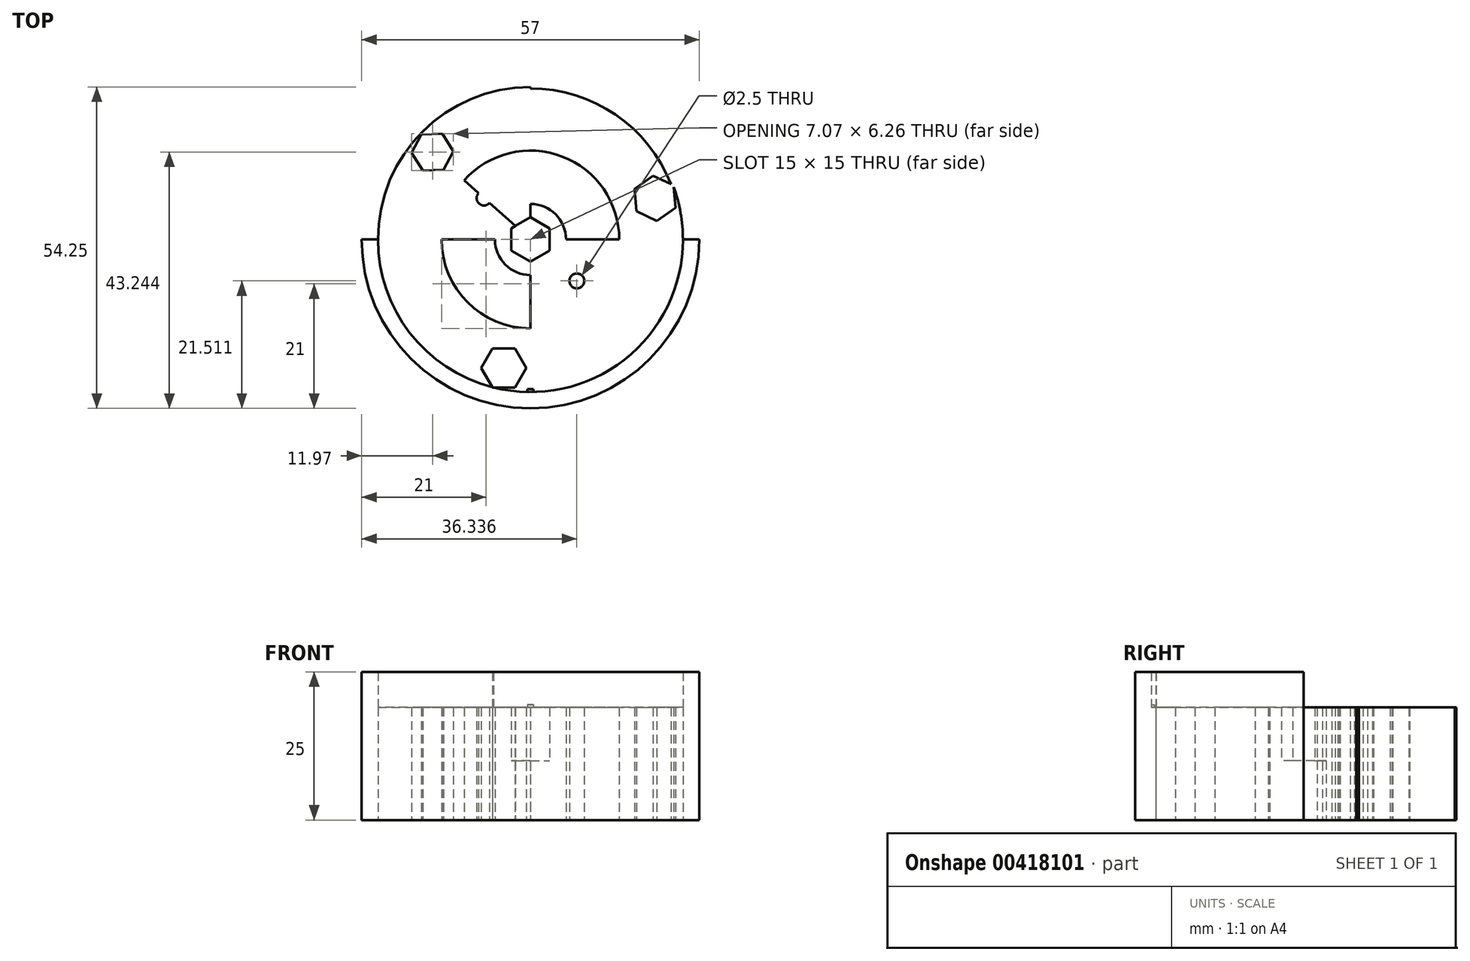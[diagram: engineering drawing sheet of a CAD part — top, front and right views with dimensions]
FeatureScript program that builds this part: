
annotation { "Feature Type Name" : "Feature", "Feature Type Description" : "" }
export const myFeature = defineFeature(function(context is Context, id is Id, definition is map)
    precondition{}
    {
        {
            var Q0;
            Q0=qCreatedBy(makeId("Top.planeOp"),FACE);
            var sketch = newSketch(context, id + "F0", { "sketchPlane" : qUnion([Q0])});
            skCircle(sketch, "E0", {"center": v(0, 0) * mm, "radius": 25.5 * mm});
            skCircle(sketch, "E1", {"center": v(0, 0) * mm, "radius": 25.75 * mm});
            skCircle(sketch, "E2", {"center": v(0, 0) * mm, "radius": 28.5 * mm});
            skLineSegment(sketch, "E3", {"start": v(0, 0) * mm, "end": v(0, 28.5) * mm});
            skLineSegment(sketch, "E4", {"start": v(0, 28.5) * mm, "end": v(0, -28.5) * mm});
            skLineSegment(sketch, "E5", {"start": v(-28.5, 0) * mm, "end": v(28.5, 0) * mm});
            skLineSegment(sketch, "E6", {"start": v(0, 0) * mm, "end": v(-4.5, -21.69) * mm});
            skLineSegment(sketch, "E7", {"start": v(-4.5, -21.69) * mm, "end": v(0, -22.62) * mm});
            skLineSegment(sketch, "E8", {"start": v(0, 0) * mm, "end": v(-16.53, 14.74) * mm});
            skLineSegment(sketch, "E9", {"start": v(-16.53, 14.74) * mm, "end": v(0, 0) * mm});
            skLineSegment(sketch, "E10", {"start": v(0, 0) * mm, "end": v(21.03, 6.94) * mm});
            skCircle(sketch, "E11", {"center": v(-4.5, -21.69) * mm, "radius": 0.75 * mm});
            skCircle(sketch, "E12", {"center": v(21.03, 6.94) * mm, "radius": 0.75 * mm});
            skCircle(sketch, "E13", {"center": v(-16.53, 14.74) * mm, "radius": 0.75 * mm});
            skCircle(sketch, "E14.cCircle", {"center": v(0, 0) * mm, "radius": 3.25 * mm, "construction": true});
            skLineSegment(sketch, "E14.0", {"start": v(3.25, 1.88) * mm, "end": v(3.25, -1.88) * mm});
            skLineSegment(sketch, "E14.1", {"start": v(3.25, -1.88) * mm, "end": v(0, -3.75) * mm});
            skLineSegment(sketch, "E14.2", {"start": v(0, -3.75) * mm, "end": v(-3.25, -1.88) * mm});
            skLineSegment(sketch, "E14.3", {"start": v(-3.25, -1.88) * mm, "end": v(-3.25, 1.88) * mm});
            skLineSegment(sketch, "E14.4", {"start": v(-3.25, 1.88) * mm, "end": v(0, 3.75) * mm});
            skLineSegment(sketch, "E14.5", {"start": v(0, 3.75) * mm, "end": v(3.25, 1.88) * mm});
            skPoint(sketch, "E14.0.midPoint", {"position": v(3.25, 0) * mm});
            skCircle(sketch, "E15", {"center": v(0, 0) * mm, "radius": 6 * mm});
            skCircle(sketch, "E16", {"center": v(0, 0) * mm, "radius": 15 * mm});
            skLineSegment(sketch, "E17", {"start": v(-9.73, -23.84) * mm, "end": v(-9.73, -26.79) * mm});
            skLineSegment(sketch, "E18", {"start": v(8.49, -27.2) * mm, "end": v(8.49, -24.31) * mm});
            skCircle(sketch, "E19.cCircle", {"center": v(-16.53, 14.74) * mm, "radius": 3.06 * mm, "construction": true});
            skLineSegment(sketch, "E19.0", {"start": v(-14.88, 17.87) * mm, "end": v(-13, 14.88) * mm});
            skLineSegment(sketch, "E19.1", {"start": v(-13, 14.88) * mm, "end": v(-14.65, 11.75) * mm});
            skLineSegment(sketch, "E19.2", {"start": v(-14.65, 11.75) * mm, "end": v(-18.18, 11.62) * mm});
            skLineSegment(sketch, "E19.3", {"start": v(-18.18, 11.62) * mm, "end": v(-20.06, 14.6) * mm});
            skLineSegment(sketch, "E19.4", {"start": v(-20.06, 14.6) * mm, "end": v(-18.41, 17.74) * mm});
            skLineSegment(sketch, "E19.5", {"start": v(-18.41, 17.74) * mm, "end": v(-14.88, 17.87) * mm});
            skPoint(sketch, "E19.0.midPoint", {"position": v(-13.94, 16.38) * mm});
            skCircle(sketch, "E20.cCircle", {"center": v(-4.5, -21.69) * mm, "radius": 3.3 * mm, "construction": true});
            skLineSegment(sketch, "E20.0", {"start": v(-6.4, -18.39) * mm, "end": v(-2.6, -18.39) * mm});
            skLineSegment(sketch, "E20.1", {"start": v(-2.6, -18.39) * mm, "end": v(-0.7, -21.69) * mm});
            skLineSegment(sketch, "E20.2", {"start": v(-0.7, -21.69) * mm, "end": v(-2.6, -24.99) * mm});
            skLineSegment(sketch, "E20.3", {"start": v(-2.6, -24.99) * mm, "end": v(-6.4, -24.99) * mm});
            skLineSegment(sketch, "E20.4", {"start": v(-6.4, -24.99) * mm, "end": v(-8.31, -21.69) * mm});
            skLineSegment(sketch, "E20.5", {"start": v(-8.31, -21.69) * mm, "end": v(-6.4, -18.39) * mm});
            skPoint(sketch, "E20.0.midPoint", {"position": v(-4.5, -18.39) * mm});
            skCircle(sketch, "E21.cCircle", {"center": v(21.03, 6.94) * mm, "radius": 3.3 * mm, "construction": true});
            skLineSegment(sketch, "E21.0", {"start": v(20.7, 10.74) * mm, "end": v(24.16, 9.12) * mm});
            skLineSegment(sketch, "E21.1", {"start": v(24.16, 9.12) * mm, "end": v(24.49, 5.33) * mm});
            skLineSegment(sketch, "E21.2", {"start": v(24.49, 5.33) * mm, "end": v(21.36, 3.15) * mm});
            skLineSegment(sketch, "E21.3", {"start": v(21.36, 3.15) * mm, "end": v(17.9, 4.76) * mm});
            skLineSegment(sketch, "E21.4", {"start": v(17.9, 4.76) * mm, "end": v(17.58, 8.56) * mm});
            skLineSegment(sketch, "E21.5", {"start": v(17.58, 8.56) * mm, "end": v(20.7, 10.74) * mm});
            skPoint(sketch, "E21.0.midPoint", {"position": v(22.43, 9.93) * mm});
            skLineSegment(sketch, "E22", {"start": v(-4.48, 4) * mm, "end": v(-11.2, 9.98) * mm});
            skLineSegment(sketch, "E23", {"start": v(-11.2, 9.98) * mm, "end": v(11.2, -9.98) * mm});
            skLineSegment(sketch, "E24", {"start": v(11.2, -9.98) * mm, "end": v(0, 0) * mm});
            skCircle(sketch, "E25", {"center": v(-7.84, 6.99) * mm, "radius": 1.25 * mm});
            skLineSegment(sketch, "E26", {"start": v(11.2, -9.98) * mm, "end": v(4.48, -4) * mm});
            skCircle(sketch, "E27", {"center": v(7.84, -6.99) * mm, "radius": 1.25 * mm});
            skLineSegment(sketch, "E28", {"start": v(-0.5, -25.74) * mm, "end": v(-0.5, -25.24) * mm});
            skLineSegment(sketch, "E29", {"start": v(-0.5, -25.24) * mm, "end": v(0, -25.24) * mm});
            skLineSegment(sketch, "E30.MirrorCS", {"start": v(0.5, -25.24) * mm, "end": v(0, -25.24) * mm});
            skLineSegment(sketch, "E31.MirrorCS", {"start": v(0.5, -25.74) * mm, "end": v(0.5, -25.24) * mm});
            skSolve(sketch);
        }
        {
            var Q0;
            {var subQ0=sQuery(id+"F0.wireOp",EDGE,"E16");var subQ1=sQuery(id+"F0.wireOp",EDGE,"E5");var subQ2=makeQuery(id+"F0.imprint","INTERSECT",VERTEX,{"disambiguationData":[OD(0.0)],"derivedFrom":[subQ1,subQ0]});Q0=makeQuery(id+"F0.imprint","IMPRINT",FACE,{"disambiguationData":[TD([[makeQuery(id+"F0.imprint","IMPRINT",EDGE,{"disambiguationData":[TD([[subQ2,-1.0]])],"derivedFrom":subQ1}),1.0]])]});}
            var Q1;
            {var subQ0=sQuery(id+"F0.wireOp",EDGE,"E4");var subQ1=sQuery(id+"F0.wireOp",EDGE,"E1");var subQ2=makeQuery(id+"F0.imprint","INTERSECT",VERTEX,{"disambiguationData":[OD(0.0)],"derivedFrom":[subQ1,subQ0]});Q1=makeQuery(id+"F0.imprint","IMPRINT",FACE,{"disambiguationData":[TD([[makeQuery(id+"F0.imprint","IMPRINT",EDGE,{"disambiguationData":[TD([[subQ2,1.0]])],"derivedFrom":subQ1}),-1.0]])]});}
            var Q2;
            {var subQ0=sQuery(id+"F0.wireOp",EDGE,"E4");var subQ1=sQuery(id+"F0.wireOp",EDGE,"E1");var subQ2=makeQuery(id+"F0.imprint","INTERSECT",VERTEX,{"disambiguationData":[OD(0.0)],"derivedFrom":[subQ1,subQ0]});Q2=makeQuery(id+"F0.imprint","IMPRINT",FACE,{"disambiguationData":[TD([[makeQuery(id+"F0.imprint","IMPRINT",EDGE,{"disambiguationData":[TD([[subQ2,-1.0]])],"derivedFrom":subQ1}),-1.0]])]});}
            var Q3;
            {var subQ0=sQuery(id+"F0.wireOp",EDGE,"E17");Q3=makeQuery(id+"F0.imprint","IMPRINT",FACE,{"disambiguationData":[TD([[makeQuery(id+"F0.imprint","IMPRINT",EDGE,{"derivedFrom":subQ0}),-1.0]])]});}
            var Q4;
            {var subQ0=sQuery(id+"F0.wireOp",EDGE,"E17");Q4=makeQuery(id+"F0.imprint","IMPRINT",FACE,{"disambiguationData":[TD([[makeQuery(id+"F0.imprint","IMPRINT",EDGE,{"derivedFrom":subQ0}),1.0]])]});}
            var Q5;
            {var subQ0=sQuery(id+"F0.wireOp",EDGE,"E18");Q5=makeQuery(id+"F0.imprint","IMPRINT",FACE,{"disambiguationData":[TD([[makeQuery(id+"F0.imprint","IMPRINT",EDGE,{"derivedFrom":subQ0}),1.0]])]});}
            var Q6;
            {var subQ0=sQuery(id+"F0.wireOp",EDGE,"E18");Q6=makeQuery(id+"F0.imprint","IMPRINT",FACE,{"disambiguationData":[TD([[makeQuery(id+"F0.imprint","IMPRINT",EDGE,{"derivedFrom":subQ0}),-1.0]])]});}
            var Q7;
            {var subQ5=sQuery(id+"F0.wireOp",EDGE,"E5");var subQ6=sQuery(id+"F0.wireOp",EDGE,"E0");var subQ7=makeQuery(id+"F0.imprint","INTERSECT",VERTEX,{"disambiguationData":[OD(1.0)],"derivedFrom":[subQ6,subQ5]});Q7=makeQuery(id+"F0.imprint","IMPRINT",FACE,{"disambiguationData":[TD([[makeQuery(id+"F0.imprint","IMPRINT",EDGE,{"disambiguationData":[TD([[subQ7,-1.0]])],"derivedFrom":subQ6}),1.0]])]});}
            var Q8;
            {var subQ2=sQuery(id+"F0.wireOp",EDGE,"E0");var subQ6=sQuery(id+"F0.wireOp",EDGE,"E5");var subQ7=makeQuery(id+"F0.imprint","INTERSECT",VERTEX,{"disambiguationData":[OD(0.0)],"derivedFrom":[subQ2,subQ6]});Q8=makeQuery(id+"F0.imprint","IMPRINT",FACE,{"disambiguationData":[TD([[makeQuery(id+"F0.imprint","IMPRINT",EDGE,{"disambiguationData":[TD([[subQ7,1.0]])],"derivedFrom":subQ2}),1.0]])]});}
            var Q9;
            {var subQ0=sQuery(id+"F0.wireOp",EDGE,"E7");var subQ1=sQuery(id+"F0.wireOp",EDGE,"E4");var subQ2=makeQuery(id+"F0.imprint","INTERSECT",VERTEX,{"derivedFrom":[subQ1,subQ0]});Q9=makeQuery(id+"F0.imprint","IMPRINT",FACE,{"disambiguationData":[TD([[makeQuery(id+"F0.imprint","IMPRINT",EDGE,{"disambiguationData":[TD([[subQ2,1.0]])],"derivedFrom":subQ1}),-1.0]])]});}
            var Q10;
            {var subQ0=sQuery(id+"F0.wireOp",EDGE,"E15");var subQ1=sQuery(id+"F0.wireOp",EDGE,"E4");var subQ2=makeQuery(id+"F0.imprint","INTERSECT",VERTEX,{"disambiguationData":[OD(1.0)],"derivedFrom":[subQ1,subQ0]});Q10=makeQuery(id+"F0.imprint","IMPRINT",FACE,{"disambiguationData":[TD([[makeQuery(id+"F0.imprint","IMPRINT",EDGE,{"disambiguationData":[TD([[subQ2,-1.0]])],"derivedFrom":subQ1}),1.0]])]});}
            var Q11;
            {var subQ0=sQuery(id+"F0.wireOp",EDGE,"E16");var subQ1=sQuery(id+"F0.wireOp",EDGE,"E4");var subQ2=makeQuery(id+"F0.imprint","INTERSECT",VERTEX,{"disambiguationData":[OD(0.0)],"derivedFrom":[subQ1,subQ0]});Q11=makeQuery(id+"F0.imprint","IMPRINT",FACE,{"disambiguationData":[TD([[makeQuery(id+"F0.imprint","IMPRINT",EDGE,{"disambiguationData":[TD([[subQ2,-1.0]])],"derivedFrom":subQ1}),-1.0]])]});}
            var Q12;
            {var subQ0=sQuery(id+"F0.wireOp",EDGE,"E14.5");Q12=makeQuery(id+"F0.imprint","IMPRINT",FACE,{"disambiguationData":[TD([[makeQuery(id+"F0.imprint","IMPRINT",EDGE,{"derivedFrom":subQ0}),1.0]])]});}
            var Q13;
            {var subQ0=sQuery(id+"F0.wireOp",EDGE,"E14.5");Q13=makeQuery(id+"F0.imprint","IMPRINT",FACE,{"disambiguationData":[TD([[makeQuery(id+"F0.imprint","IMPRINT",EDGE,{"derivedFrom":subQ0}),1.0]])]});}
            var Q14;
            {var subQ0=sQuery(id+"F0.wireOp",EDGE,"E14.1");Q14=makeQuery(id+"F0.imprint","IMPRINT",FACE,{"disambiguationData":[TD([[makeQuery(id+"F0.imprint","IMPRINT",EDGE,{"derivedFrom":subQ0}),1.0]])]});}
            var Q15;
            {var subQ0=sQuery(id+"F0.wireOp",EDGE,"E14.1");Q15=makeQuery(id+"F0.imprint","IMPRINT",FACE,{"disambiguationData":[TD([[makeQuery(id+"F0.imprint","IMPRINT",EDGE,{"derivedFrom":subQ0}),1.0]])]});}
            var Q16;
            {var subQ3=sQuery(id+"F0.wireOp",EDGE,"E5");var subQ7=sQuery(id+"F0.wireOp",EDGE,"E15");var subQ9=makeQuery(id+"F0.imprint","INTERSECT",VERTEX,{"disambiguationData":[OD(0.0)],"derivedFrom":[subQ3,subQ7]});Q16=makeQuery(id+"F0.imprint","IMPRINT",FACE,{"disambiguationData":[TD([[makeQuery(id+"F0.imprint","IMPRINT",EDGE,{"disambiguationData":[TD([[subQ9,-1.0]])],"derivedFrom":subQ3}),-1.0]])]});}
            var Q17;
            {var subQ0=sQuery(id+"F0.wireOp",EDGE,"E14.2");var subQ5=sQuery(id+"F0.wireOp",EDGE,"E6");var subQ6=makeQuery(id+"F0.imprint","INTERSECT",VERTEX,{"derivedFrom":[subQ5,subQ0]});Q17=makeQuery(id+"F0.imprint","IMPRINT",FACE,{"disambiguationData":[TD([[makeQuery(id+"F0.imprint","IMPRINT",EDGE,{"disambiguationData":[TD([[subQ6,-1.0]])],"derivedFrom":subQ5}),1.0]])]});}
            var Q18;
            {var subQ3=sQuery(id+"F0.wireOp",EDGE,"E5");var subQ7=sQuery(id+"F0.wireOp",EDGE,"E15");var subQ9=makeQuery(id+"F0.imprint","INTERSECT",VERTEX,{"disambiguationData":[OD(0.0)],"derivedFrom":[subQ3,subQ7]});Q18=makeQuery(id+"F0.imprint","IMPRINT",FACE,{"disambiguationData":[TD([[makeQuery(id+"F0.imprint","IMPRINT",EDGE,{"disambiguationData":[TD([[subQ9,-1.0]])],"derivedFrom":subQ3}),-1.0]])]});}
            var Q19;
            {var subQ5=sQuery(id+"F0.wireOp",EDGE,"E15");var subQ6=sQuery(id+"F0.wireOp",EDGE,"E5");var subQ7=makeQuery(id+"F0.imprint","INTERSECT",VERTEX,{"disambiguationData":[OD(0.0)],"derivedFrom":[subQ6,subQ5]});Q19=makeQuery(id+"F0.imprint","IMPRINT",FACE,{"disambiguationData":[TD([[makeQuery(id+"F0.imprint","IMPRINT",EDGE,{"disambiguationData":[TD([[subQ7,-1.0]])],"derivedFrom":subQ6}),1.0]])]});}
            var Q20;
            {var subQ3=sQuery(id+"F0.wireOp",EDGE,"E15");var subQ5=sQuery(id+"F0.wireOp",EDGE,"E9");var subQ6=makeQuery(id+"F0.imprint","INTERSECT",VERTEX,{"derivedFrom":[subQ5,subQ3]});Q20=makeQuery(id+"F0.imprint","IMPRINT",FACE,{"disambiguationData":[TD([[makeQuery(id+"F0.imprint","IMPRINT",EDGE,{"disambiguationData":[TD([[subQ6,-1.0]])],"derivedFrom":subQ5}),1.0]])]});}
            var Q21;
            {var subQ0=sQuery(id+"F0.wireOp",EDGE,"E14.0");var subQ1=sQuery(id+"F0.wireOp",EDGE,"E5");var subQ2=makeQuery(id+"F0.imprint","INTERSECT",VERTEX,{"derivedFrom":[subQ1,subQ0]});Q21=makeQuery(id+"F0.imprint","IMPRINT",FACE,{"disambiguationData":[TD([[makeQuery(id+"F0.imprint","IMPRINT",EDGE,{"disambiguationData":[TD([[subQ2,-1.0]])],"derivedFrom":subQ1}),1.0]])]});}
            var Q22;
            {var subQ0=sQuery(id+"F0.wireOp",EDGE,"E4");var subQ1=sQuery(id+"F0.wireOp",EDGE,"E0");var subQ2=makeQuery(id+"F0.imprint","INTERSECT",VERTEX,{"disambiguationData":[OD(0.0)],"derivedFrom":[subQ1,subQ0]});Q22=makeQuery(id+"F0.imprint","IMPRINT",FACE,{"disambiguationData":[TD([[makeQuery(id+"F0.imprint","IMPRINT",EDGE,{"disambiguationData":[TD([[subQ2,1.0]])],"derivedFrom":subQ1}),-1.0]])]});}
            var Q23;
            {var subQ1=sQuery(id+"F0.wireOp",EDGE,"E0");var subQ6=sQuery(id+"F0.wireOp",EDGE,"E5");var subQ8=makeQuery(id+"F0.imprint","INTERSECT",VERTEX,{"disambiguationData":[OD(0.0)],"derivedFrom":[subQ1,subQ6]});Q23=makeQuery(id+"F0.imprint","IMPRINT",FACE,{"disambiguationData":[TD([[makeQuery(id+"F0.imprint","IMPRINT",EDGE,{"disambiguationData":[TD([[subQ8,1.0]])],"derivedFrom":subQ1}),-1.0]])]});}
            var Q24;
            {var subQ2=sQuery(id+"F0.wireOp",EDGE,"E5");var subQ5=sQuery(id+"F0.wireOp",EDGE,"E0");var subQ8=makeQuery(id+"F0.imprint","INTERSECT",VERTEX,{"disambiguationData":[OD(1.0)],"derivedFrom":[subQ5,subQ2]});Q24=makeQuery(id+"F0.imprint","IMPRINT",FACE,{"disambiguationData":[TD([[makeQuery(id+"F0.imprint","IMPRINT",EDGE,{"disambiguationData":[TD([[subQ8,-1.0]])],"derivedFrom":subQ5}),-1.0]])]});}
            var Q25;
            {var subQ0=sQuery(id+"F0.wireOp",EDGE,"E4");var subQ1=sQuery(id+"F0.wireOp",EDGE,"E0");var subQ2=makeQuery(id+"F0.imprint","INTERSECT",VERTEX,{"disambiguationData":[OD(0.0)],"derivedFrom":[subQ1,subQ0]});Q25=makeQuery(id+"F0.imprint","IMPRINT",FACE,{"disambiguationData":[TD([[makeQuery(id+"F0.imprint","IMPRINT",EDGE,{"disambiguationData":[TD([[subQ2,-1.0]])],"derivedFrom":subQ1}),-1.0]])]});}
            var Q26;
            {var subQ11=sQuery(id+"F0.wireOp",EDGE,"E19.0");Q26=makeQuery(id+"F0.imprint","IMPRINT",FACE,{"disambiguationData":[TD([[makeQuery(id+"F0.imprint","IMPRINT",EDGE,{"derivedFrom":subQ11}),1.0]])]});}
            var Q27;
            {var subQ7=sQuery(id+"F0.wireOp",EDGE,"E21.5");Q27=makeQuery(id+"F0.imprint","IMPRINT",FACE,{"disambiguationData":[TD([[makeQuery(id+"F0.imprint","IMPRINT",EDGE,{"derivedFrom":subQ7}),1.0]])]});}
            var Q28;
            {var subQ0=sQuery(id+"F0.wireOp",EDGE,"E20.2");var subQ1=sQuery(id+"F0.wireOp",EDGE,"E0");var subQ2=makeQuery(id+"F0.imprint","INTERSECT",VERTEX,{"derivedFrom":[subQ1,subQ0]});Q28=makeQuery(id+"F0.imprint","IMPRINT",FACE,{"disambiguationData":[TD([[makeQuery(id+"F0.imprint","IMPRINT",EDGE,{"disambiguationData":[TD([[subQ2,-1.0]])],"derivedFrom":subQ1}),1.0]])]});}
            var Q29;
            {var subQ12=sQuery(id+"F0.wireOp",EDGE,"E19.2");Q29=makeQuery(id+"F0.imprint","IMPRINT",FACE,{"disambiguationData":[TD([[makeQuery(id+"F0.imprint","IMPRINT",EDGE,{"derivedFrom":subQ12}),1.0]])]});}
            var Q30;
            {var subQ0=sQuery(id+"F0.wireOp",EDGE,"E19.4");var subQ1=sQuery(id+"F0.wireOp",EDGE,"E0");var subQ2=makeQuery(id+"F0.imprint","INTERSECT",VERTEX,{"derivedFrom":[subQ1,subQ0]});Q30=makeQuery(id+"F0.imprint","IMPRINT",FACE,{"disambiguationData":[TD([[makeQuery(id+"F0.imprint","IMPRINT",EDGE,{"disambiguationData":[TD([[subQ2,-1.0]])],"derivedFrom":subQ1}),-1.0]])]});}
            var Q31;
            {var subQ1=sQuery(id+"F0.wireOp",EDGE,"E20.2");var subQ3=sQuery(id+"F0.wireOp",EDGE,"E0");var subQ4=makeQuery(id+"F0.imprint","INTERSECT",VERTEX,{"derivedFrom":[subQ3,subQ1]});Q31=makeQuery(id+"F0.imprint","IMPRINT",FACE,{"disambiguationData":[TD([[makeQuery(id+"F0.imprint","IMPRINT",EDGE,{"disambiguationData":[TD([[subQ4,-1.0]])],"derivedFrom":subQ3}),-1.0]])]});}
            var Q32;
            {var subQ11=sQuery(id+"F0.wireOp",EDGE,"E21.3");Q32=makeQuery(id+"F0.imprint","IMPRINT",FACE,{"disambiguationData":[TD([[makeQuery(id+"F0.imprint","IMPRINT",EDGE,{"derivedFrom":subQ11}),1.0]])]});}
            var Q33;
            {var subQ0=sQuery(id+"F0.wireOp",EDGE,"E21.2");var subQ6=sQuery(id+"F0.wireOp",EDGE,"E0");var subQ9=makeQuery(id+"F0.imprint","INTERSECT",VERTEX,{"derivedFrom":[subQ6,subQ0]});Q33=makeQuery(id+"F0.imprint","IMPRINT",FACE,{"disambiguationData":[TD([[makeQuery(id+"F0.imprint","IMPRINT",EDGE,{"disambiguationData":[TD([[subQ9,1.0]])],"derivedFrom":subQ6}),-1.0]])]});}
            var Q34;
            {var subQ1=sQuery(id+"F0.wireOp",EDGE,"E4");var subQ3=sQuery(id+"F0.wireOp",EDGE,"E15");var subQ4=makeQuery(id+"F0.imprint","INTERSECT",VERTEX,{"disambiguationData":[OD(0.0)],"derivedFrom":[subQ1,subQ3]});Q34=makeQuery(id+"F0.imprint","IMPRINT",FACE,{"disambiguationData":[TD([[makeQuery(id+"F0.imprint","IMPRINT",EDGE,{"disambiguationData":[TD([[subQ4,-1.0]])],"derivedFrom":subQ3}),1.0]])]});}
            var Q35;
            {var subQ3=sQuery(id+"F0.wireOp",EDGE,"E5");var subQ6=sQuery(id+"F0.wireOp",EDGE,"E14.0");var subQ9=makeQuery(id+"F0.imprint","INTERSECT",VERTEX,{"derivedFrom":[subQ3,subQ6]});Q35=makeQuery(id+"F0.imprint","IMPRINT",FACE,{"disambiguationData":[TD([[makeQuery(id+"F0.imprint","IMPRINT",EDGE,{"disambiguationData":[TD([[subQ9,-1.0]])],"derivedFrom":subQ3}),-1.0]])]});}
            var Q36;
            {var subQ3=sQuery(id+"F0.wireOp",EDGE,"E5");var subQ5=sQuery(id+"F0.wireOp",EDGE,"E15");var subQ7=makeQuery(id+"F0.imprint","INTERSECT",VERTEX,{"disambiguationData":[OD(1.0)],"derivedFrom":[subQ3,subQ5]});Q36=makeQuery(id+"F0.imprint","IMPRINT",FACE,{"disambiguationData":[TD([[makeQuery(id+"F0.imprint","IMPRINT",EDGE,{"disambiguationData":[TD([[subQ7,-1.0]])],"derivedFrom":subQ3}),-1.0]])]});}
            var Q37;
            {var subQ0=sQuery(id+"F0.wireOp",EDGE,"E20.3");var subQ1=sQuery(id+"F0.wireOp",EDGE,"E0");var subQ2=makeQuery(id+"F0.imprint","INTERSECT",VERTEX,{"derivedFrom":[subQ1,subQ0]});Q37=makeQuery(id+"F0.imprint","IMPRINT",FACE,{"disambiguationData":[TD([[makeQuery(id+"F0.imprint","IMPRINT",EDGE,{"disambiguationData":[TD([[subQ2,-1.0]])],"derivedFrom":subQ1}),-1.0]])]});}
            var Q38;
            {var subQ0=sQuery(id+"F0.wireOp",EDGE,"E21.1");var subQ1=sQuery(id+"F0.wireOp",EDGE,"E0");var subQ2=makeQuery(id+"F0.imprint","INTERSECT",VERTEX,{"derivedFrom":[subQ1,subQ0]});Q38=makeQuery(id+"F0.imprint","IMPRINT",FACE,{"disambiguationData":[TD([[makeQuery(id+"F0.imprint","IMPRINT",EDGE,{"disambiguationData":[TD([[subQ2,1.0]])],"derivedFrom":subQ1}),-1.0]])]});}
            var Q39;
            {var subQ7=sQuery(id+"F0.wireOp",EDGE,"E29");Q39=makeQuery(id+"F0.imprint","IMPRINT",FACE,{"disambiguationData":[TD([[makeQuery(id+"F0.imprint","IMPRINT",EDGE,{"derivedFrom":subQ7}),1.0]])]});}
            var Q40;
            {var subQ5=sQuery(id+"F0.wireOp",EDGE,"LtNLRzwu-Uu6k-sooV-pEHR-ru2ubIBkx8k7");Q40=makeQuery(id+"F0.imprint","IMPRINT",FACE,{"disambiguationData":[TD([[makeQuery(id+"F0.imprint","IMPRINT",EDGE,{"derivedFrom":subQ5}),-1.0]])]});}
            var Q41;
            {var subQ5=sQuery(id+"F0.wireOp",EDGE,"431a47f9-fcb9-445b-ae95-e29a805c047c0.MirrorCS");Q41=makeQuery(id+"F0.imprint","IMPRINT",FACE,{"disambiguationData":[TD([[makeQuery(id+"F0.imprint","IMPRINT",EDGE,{"derivedFrom":subQ5}),1.0]])]});}
            var Q42;
            {var subQ0=sQuery(id+"F0.wireOp",EDGE,"E4");var subQ1=sQuery(id+"F0.wireOp",EDGE,"E0");var subQ2=makeQuery(id+"F0.imprint","INTERSECT",VERTEX,{"disambiguationData":[OD(1.0)],"derivedFrom":[subQ1,subQ0]});Q42=makeQuery(id+"F0.imprint","IMPRINT",FACE,{"disambiguationData":[TD([[makeQuery(id+"F0.imprint","IMPRINT",EDGE,{"disambiguationData":[TD([[subQ2,-1.0]])],"derivedFrom":subQ1}),-1.0]])]});}
            var Q43;
            {var subQ0=sQuery(id+"F0.wireOp",EDGE,"E28");var subQ1=sQuery(id+"F0.wireOp",EDGE,"E0");var subQ2=makeQuery(id+"F0.imprint","INTERSECT",VERTEX,{"derivedFrom":[subQ1,subQ0]});Q43=makeQuery(id+"F0.imprint","IMPRINT",FACE,{"disambiguationData":[TD([[makeQuery(id+"F0.imprint","IMPRINT",EDGE,{"disambiguationData":[TD([[subQ2,-1.0]])],"derivedFrom":subQ1}),-1.0]])]});}
            extrude(context, id + "F1", {"entities" : qUnion([Q0, Q1, Q2, Q3, Q4, Q5, Q6, Q7, Q8, Q9, Q10, Q11, Q12, Q13, Q14, Q15, Q16, Q17, Q18, Q19, Q20, Q21, Q22, Q23, Q24, Q25, Q26, Q27, Q28, Q29, Q30, Q31, Q32, Q33, Q34, Q35, Q36, Q37, Q38, Q39, Q40, Q41, Q42, Q43]), "depth" : 19 * mm});
        }
        {
            var Q0;
            {var subQ0=sQuery(id+"F0.wireOp",EDGE,"E4");var subQ1=sQuery(id+"F0.wireOp",EDGE,"E1");var subQ2=makeQuery(id+"F0.imprint","INTERSECT",VERTEX,{"disambiguationData":[OD(0.0)],"derivedFrom":[subQ1,subQ0]});Q0=makeQuery(id+"F0.imprint","IMPRINT",FACE,{"disambiguationData":[TD([[makeQuery(id+"F0.imprint","IMPRINT",EDGE,{"disambiguationData":[TD([[subQ2,1.0]])],"derivedFrom":subQ1}),-1.0]])]});}
            var Q1;
            {var subQ0=sQuery(id+"F0.wireOp",EDGE,"E5");var subQ1=sQuery(id+"F0.wireOp",EDGE,"E1");var subQ2=makeQuery(id+"F0.imprint","INTERSECT",VERTEX,{"disambiguationData":[OD(0.0)],"derivedFrom":[subQ1,subQ0]});Q1=makeQuery(id+"F0.imprint","IMPRINT",FACE,{"disambiguationData":[TD([[makeQuery(id+"F0.imprint","IMPRINT",EDGE,{"disambiguationData":[TD([[subQ2,1.0]])],"derivedFrom":subQ1}),-1.0]])]});}
            var Q2;
            {var subQ0=sQuery(id+"F0.wireOp",EDGE,"E5");var subQ1=sQuery(id+"F0.wireOp",EDGE,"E1");var subQ2=makeQuery(id+"F0.imprint","INTERSECT",VERTEX,{"disambiguationData":[OD(1.0)],"derivedFrom":[subQ1,subQ0]});Q2=makeQuery(id+"F0.imprint","IMPRINT",FACE,{"disambiguationData":[TD([[makeQuery(id+"F0.imprint","IMPRINT",EDGE,{"disambiguationData":[TD([[subQ2,-1.0]])],"derivedFrom":subQ1}),-1.0]])]});}
            var Q3;
            {var subQ0=sQuery(id+"F0.wireOp",EDGE,"E4");var subQ1=sQuery(id+"F0.wireOp",EDGE,"E1");var subQ2=makeQuery(id+"F0.imprint","INTERSECT",VERTEX,{"disambiguationData":[OD(0.0)],"derivedFrom":[subQ1,subQ0]});Q3=makeQuery(id+"F0.imprint","IMPRINT",FACE,{"disambiguationData":[TD([[makeQuery(id+"F0.imprint","IMPRINT",EDGE,{"disambiguationData":[TD([[subQ2,-1.0]])],"derivedFrom":subQ1}),-1.0]])]});}
            extrude(context, id + "F2", {"entities" : qUnion([Q0, Q1, Q2, Q3]), "operationType" : NewBodyOperationType.ADD, "depth" : 25 * mm});
        }
        {
            var Q0;
            {var subQ3=sQuery(id+"F0.wireOp",EDGE,"E14.3");var subQ5=sQuery(id+"F0.wireOp",EDGE,"E14.2");var subQ7=makeQuery(id+"F0.imprint","INTERSECT",VERTEX,{"derivedFrom":[subQ5,subQ3]});Q0=makeQuery(id+"F0.imprint","IMPRINT",FACE,{"disambiguationData":[TD([[makeQuery(id+"F0.imprint","IMPRINT",EDGE,{"disambiguationData":[TD([[subQ7,1.0]])],"derivedFrom":subQ5}),-1.0]])]});}
            var Q1;
            {var subQ3=sQuery(id+"F0.wireOp",EDGE,"E14.3");var subQ5=sQuery(id+"F0.wireOp",EDGE,"E14.4");var subQ6=makeQuery(id+"F0.imprint","INTERSECT",VERTEX,{"derivedFrom":[subQ3,subQ5]});Q1=makeQuery(id+"F0.imprint","IMPRINT",FACE,{"disambiguationData":[TD([[makeQuery(id+"F0.imprint","IMPRINT",EDGE,{"disambiguationData":[TD([[subQ6,1.0]])],"derivedFrom":subQ3}),-1.0]])]});}
            var Q2;
            {var subQ0=sQuery(id+"F0.wireOp",EDGE,"E23");var subQ3=sQuery(id+"F0.wireOp",EDGE,"E14.4");var subQ5=makeQuery(id+"F0.imprint","INTERSECT",VERTEX,{"derivedFrom":[subQ3,subQ0]});Q2=makeQuery(id+"F0.imprint","IMPRINT",FACE,{"disambiguationData":[TD([[makeQuery(id+"F0.imprint","IMPRINT",EDGE,{"disambiguationData":[TD([[subQ5,-1.0]])],"derivedFrom":subQ3}),-1.0]])]});}
            var Q3;
            {var subQ3=sQuery(id+"F0.wireOp",EDGE,"E14.5");Q3=makeQuery(id+"F0.imprint","IMPRINT",FACE,{"disambiguationData":[TD([[makeQuery(id+"F0.imprint","IMPRINT",EDGE,{"derivedFrom":subQ3}),-1.0]])]});}
            var Q4;
            {var subQ1=sQuery(id+"F0.wireOp",EDGE,"E5");var subQ3=sQuery(id+"F0.wireOp",EDGE,"E14.0");var subQ4=makeQuery(id+"F0.imprint","INTERSECT",VERTEX,{"derivedFrom":[subQ1,subQ3]});Q4=makeQuery(id+"F0.imprint","IMPRINT",FACE,{"disambiguationData":[TD([[makeQuery(id+"F0.imprint","IMPRINT",EDGE,{"disambiguationData":[TD([[subQ4,1.0]])],"derivedFrom":subQ3}),-1.0]])]});}
            var Q5;
            {var subQ0=sQuery(id+"F0.wireOp",EDGE,"E24");var subQ3=sQuery(id+"F0.wireOp",EDGE,"E14.1");var subQ5=makeQuery(id+"F0.imprint","INTERSECT",VERTEX,{"derivedFrom":[subQ3,subQ0]});Q5=makeQuery(id+"F0.imprint","IMPRINT",FACE,{"disambiguationData":[TD([[makeQuery(id+"F0.imprint","IMPRINT",EDGE,{"disambiguationData":[TD([[subQ5,-1.0]])],"derivedFrom":subQ3}),-1.0]])]});}
            var Q6;
            {var subQ3=sQuery(id+"F0.wireOp",EDGE,"E14.0");var subQ5=sQuery(id+"F0.wireOp",EDGE,"E14.1");var subQ6=makeQuery(id+"F0.imprint","INTERSECT",VERTEX,{"derivedFrom":[subQ3,subQ5]});Q6=makeQuery(id+"F0.imprint","IMPRINT",FACE,{"disambiguationData":[TD([[makeQuery(id+"F0.imprint","IMPRINT",EDGE,{"disambiguationData":[TD([[subQ6,1.0]])],"derivedFrom":subQ3}),-1.0]])]});}
            var Q7;
            {var subQ0=sQuery(id+"F0.wireOp",EDGE,"E6");var subQ3=sQuery(id+"F0.wireOp",EDGE,"E14.2");var subQ5=makeQuery(id+"F0.imprint","INTERSECT",VERTEX,{"derivedFrom":[subQ0,subQ3]});Q7=makeQuery(id+"F0.imprint","IMPRINT",FACE,{"disambiguationData":[TD([[makeQuery(id+"F0.imprint","IMPRINT",EDGE,{"disambiguationData":[TD([[subQ5,1.0]])],"derivedFrom":subQ3}),-1.0]])]});}
            extrude(context, id + "F3", {"entities" : qUnion([Q0, Q1, Q2, Q3, Q4, Q5, Q6, Q7]), "operationType" : NewBodyOperationType.ADD, "depth" : 10 * mm});
        }
        {
            var Q0;
            {var subQ0=sQuery(id+"F0.wireOp",EDGE,"E28");var subQ1=sQuery(id+"F0.wireOp",EDGE,"E0");var subQ2=makeQuery(id+"F0.imprint","INTERSECT",VERTEX,{"derivedFrom":[subQ1,subQ0]});Q0=makeQuery(id+"F0.imprint","IMPRINT",FACE,{"disambiguationData":[TD([[makeQuery(id+"F0.imprint","IMPRINT",EDGE,{"disambiguationData":[TD([[subQ2,-1.0]])],"derivedFrom":subQ1}),-1.0]])]});}
            var Q1;
            {var subQ0=sQuery(id+"F0.wireOp",EDGE,"E4");var subQ1=sQuery(id+"F0.wireOp",EDGE,"E0");var subQ2=makeQuery(id+"F0.imprint","INTERSECT",VERTEX,{"disambiguationData":[OD(1.0)],"derivedFrom":[subQ1,subQ0]});Q1=makeQuery(id+"F0.imprint","IMPRINT",FACE,{"disambiguationData":[TD([[makeQuery(id+"F0.imprint","IMPRINT",EDGE,{"disambiguationData":[TD([[subQ2,-1.0]])],"derivedFrom":subQ1}),-1.0]])]});}
            var Q2;
            {var subQ5=sQuery(id+"F0.wireOp",EDGE,"E30.MirrorCS");Q2=makeQuery(id+"F0.imprint","IMPRINT",FACE,{"disambiguationData":[TD([[makeQuery(id+"F0.imprint","IMPRINT",EDGE,{"derivedFrom":subQ5}),1.0]])]});}
            var Q3;
            {var subQ5=sQuery(id+"F0.wireOp",EDGE,"E29");Q3=makeQuery(id+"F0.imprint","IMPRINT",FACE,{"disambiguationData":[TD([[makeQuery(id+"F0.imprint","IMPRINT",EDGE,{"derivedFrom":subQ5}),-1.0]])]});}
            extrude(context, id + "F4", {"entities" : qUnion([Q0, Q1, Q2, Q3]), "operationType" : NewBodyOperationType.ADD, "depth" : 19.5 * mm});
        }
    });
